# Revit family: Door_Overhead-Sectional_WayneDalton_Thermospan-High-Lift
name_source: partatom
category: Doors
revit_build: Autodesk Revit 2014 (Build: 20130308_1515(x64)
units: mm (PartAtom-declared; Revit-internal decimal feet)

## types (4) — shared parameters
Analytic Construction = <None>
Assembly Code = B2030410
Fire Performance = Flash Ignition 734 F  ;  Self Ignition 950
Fire Rating = as Specified
Function = Interior
Heat Transfer Coefficient (U) = 0.1 BTU/(h·ft²·°F)
Height = 0' - 0"
Keynote = 08 36 13
Manufacturer = Wayne Dalton
Manufacturer Website = http://www.wayne-dalton.com
Operation = as Specified
Product Data = http://www.arcat.com
Revision = R1_2016-11
Rough Height = 0' - 0"
Rough Width = 0' - 0"
Sales Information = http://www.wayne-dalton.com
Solar Heat Gain Coefficient = 0.1
SpecWizard = http://www.arcat.com
Specification = http://www.arcat.com
Thermal Resistance (R) = 0.1000 (h·ft²·°F)/BTU
Thickness = 0' - 0"
URL = http://www.wayne-dalton.com
Visual Light Transmittance = 0.1
Wall Closure = By host
Width = 0' - 0"
zero-valued in all types: Cost, Expected Lifespan (Years), Maintenance Schedule (Months), STC Rating, Warranty Duration (Years)

## per-type parameters (varying)
| type | Air Infiltration | Description | Max Height | Max Width | Panel Thickness | R-Value | Standards Conformance | U Value |
| Thermospan 150 | 0.23 cfm/ft^2 at 15 MPH | Wayne Dalton Insulated Overhead Sectional Door - Thermospan 150 as Specified | 20' - 1" | 26' - 2" | 0' - 1 3/8" | 14.16 | STC Class 22  ;  OITC Class 19  ;  ASTM E 84 Class A  ;  UBC 17-5 | 0.07 |
| Thermospan 125 | as Specified | Wayne Dalton Insulated Overhead Sectional Door - Thermospan 125 as Specified | 16' - 1" | 16' - 2" | 0' - 0 7/8" | 10.79 | STC Class 21  ;  OITC Class 18  ;  ASTM E 84 Class A  ;  UBC 17-5 | 0.093 |
| Thermospan 200-20 | 0.07 cfm/ft^2 | Wayne Dalton Insulated Overhead Sectional Door - Thermospan 200-200 as Specified | 16' - 1" | 24' - 2" | 0' - 2" | 17.5 | STC Class 22  ;  OITC Class 19  ;  ASTM E 84 Class A  ;  UBC 17-5 | 0.57 |
| Thermospan 200 | 0.07 cfm/ft^2 | Wayne Dalton Insulated Overhead Sectional Door - Thermospan 200 as Specified | 32' - 1" | 40' - 2" | 0' - 2" | 17.5 | STC Class 22  ;  OITC Class 19  ;  ASTM E 84 Class A  ;  UBC 17-5 | 0.57 |

note: column(s) folded — value = type name in every type: Model

## geometry (parser evidence)
native form markers: Sweep x27
no freeform markers — native parametric forms only
